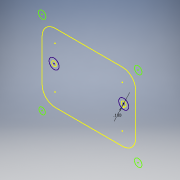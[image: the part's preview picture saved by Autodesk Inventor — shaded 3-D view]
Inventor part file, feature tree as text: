
AUTODESK INVENTOR PART (.ipt)
format: ipt  version: 2016 (Build 200138000, 138)  size: 87,040 bytes
history: native  units: in
note: dims shown in document units (in); Inventor stores cm internally (conversion verified against a paired STEP export)
features: reference x10, sketch x1
ambient origin geometry x8: Origin, YZ Plane, XZ Plane, XY Plane, X Axis, Y Axis, Z Axis, Center Point
feature tree (11):
  sketch  "Sketch1"  dims[d0=0.1in]
  reference  "Reference1"
  reference  "Reference2"
  reference  "Reference3"
  reference  "Reference4"
  reference  "Reference5"
  reference  "Reference6"
  reference  "Reference7"
  reference  "Reference8"
  reference  "Reference9"
  reference  "Reference10"
